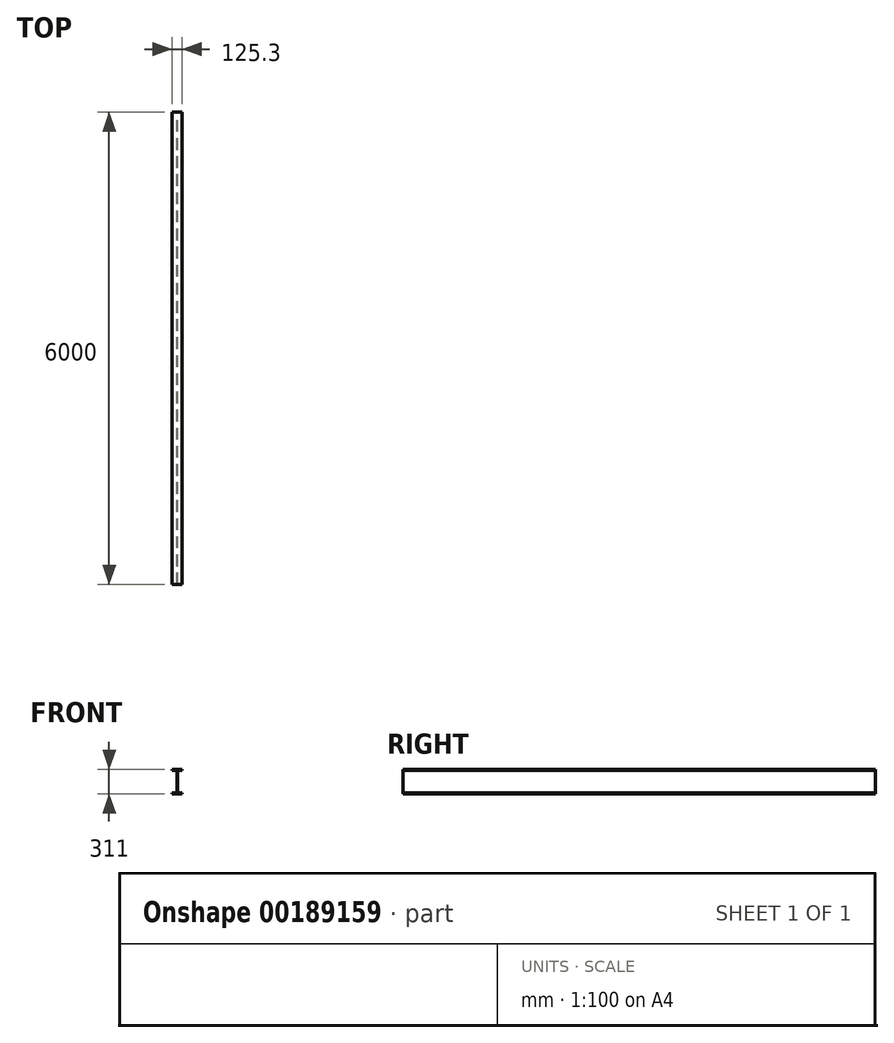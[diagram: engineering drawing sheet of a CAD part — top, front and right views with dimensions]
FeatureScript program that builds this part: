
annotation { "Feature Type Name" : "Feature", "Feature Type Description" : "" }
export const myFeature = defineFeature(function(context is Context, id is Id, definition is map)
    precondition{}
    {
        {
            var Q0;
            Q0=qCreatedBy(makeId("Front.planeOp"),FACE);
            var sketch = newSketch(context, id + "F0", { "sketchPlane" : qUnion([Q0])});
            skLineSegment(sketch, "E0", {"start": v(0, 195.7) * mm, "end": v(0, -206.2) * mm, "construction": true});
            skLineSegment(sketch, "E1", {"start": v(0, 181.95) * mm, "end": v(-62.65, 181.95) * mm});
            skLineSegment(sketch, "E2", {"start": v(-62.65, 181.95) * mm, "end": v(-62.65, 167.95) * mm});
            skLineSegment(sketch, "E3", {"start": v(-62.65, 167.95) * mm, "end": v(-13.4, 167.95) * mm});
            skLineSegment(sketch, "E4", {"start": v(-4.5, 159.05) * mm, "end": v(-4.5, -106.15) * mm});
            skLineSegment(sketch, "E5", {"start": v(-13.4, -115.05) * mm, "end": v(-62.65, -115.05) * mm});
            skLineSegment(sketch, "E6", {"start": v(-62.65, -115.05) * mm, "end": v(-62.65, -129.05) * mm});
            skLineSegment(sketch, "E7", {"start": v(-62.65, -129.05) * mm, "end": v(0, -129.05) * mm});
            skLineSegment(sketch, "E8.MirrorCS", {"start": v(62.65, 167.95) * mm, "end": v(13.4, 167.95) * mm});
            skLineSegment(sketch, "E9.MirrorCS", {"start": v(0, 181.95) * mm, "end": v(62.65, 181.95) * mm});
            skLineSegment(sketch, "E10.MirrorCS", {"start": v(62.65, -115.05) * mm, "end": v(62.65, -129.05) * mm});
            skLineSegment(sketch, "E11.MirrorCS", {"start": v(4.5, 159.05) * mm, "end": v(4.5, -106.15) * mm});
            skLineSegment(sketch, "E12.MirrorCS", {"start": v(13.4, -115.05) * mm, "end": v(62.65, -115.05) * mm});
            skLineSegment(sketch, "E13.MirrorCS", {"start": v(62.65, 181.95) * mm, "end": v(62.65, 167.95) * mm});
            skLineSegment(sketch, "E14.MirrorCS", {"start": v(62.65, -129.05) * mm, "end": v(0, -129.05) * mm});
            skPoint(sketch, "E15.visualSharp", {"position": v(-4.5, 167.95) * mm});
            skArc(sketch, "E15.filletArc", {"start": v(-4.5, 159.05) * mm, "mid": v(-7.1, 165.35) * mm, "end": v(-13.4, 167.95) * mm});
            skPoint(sketch, "E16.visualSharp", {"position": v(4.5, 167.95) * mm});
            skArc(sketch, "E16.filletArc", {"start": v(13.4, 167.95) * mm, "mid": v(7.1, 165.35) * mm, "end": v(4.5, 159.05) * mm});
            skPoint(sketch, "E17.visualSharp", {"position": v(-4.5, -115.05) * mm});
            skArc(sketch, "E17.filletArc", {"start": v(-13.4, -115.05) * mm, "mid": v(-7.1, -112.44) * mm, "end": v(-4.5, -106.15) * mm});
            skPoint(sketch, "E18.visualSharp", {"position": v(4.5, -115.05) * mm});
            skArc(sketch, "E18.filletArc", {"start": v(4.5, -106.15) * mm, "mid": v(7.1, -112.44) * mm, "end": v(13.4, -115.05) * mm});
            skSolve(sketch);
        }
        {
            assignVariable(context, id + "F1", {"name" : "Jib_Length", "anyValue" : 6000});
        }
        {
            var Q0;
            Q0=makeQuery(id+"F0.imprint","IMPRINT",FACE,{"disambiguationData":[TD([[makeQuery(id+"F0.imprint","IMPRINT",EDGE,{"derivedFrom":sQuery(id+"F0.wireOp",EDGE,"E1")}),1.0]])]});
            extrude(context, id + "F2", {"entities" : qUnion([Q0]), "depth" : (getVariable(context, 'Jib_Length')) * mm});
        }
    });
